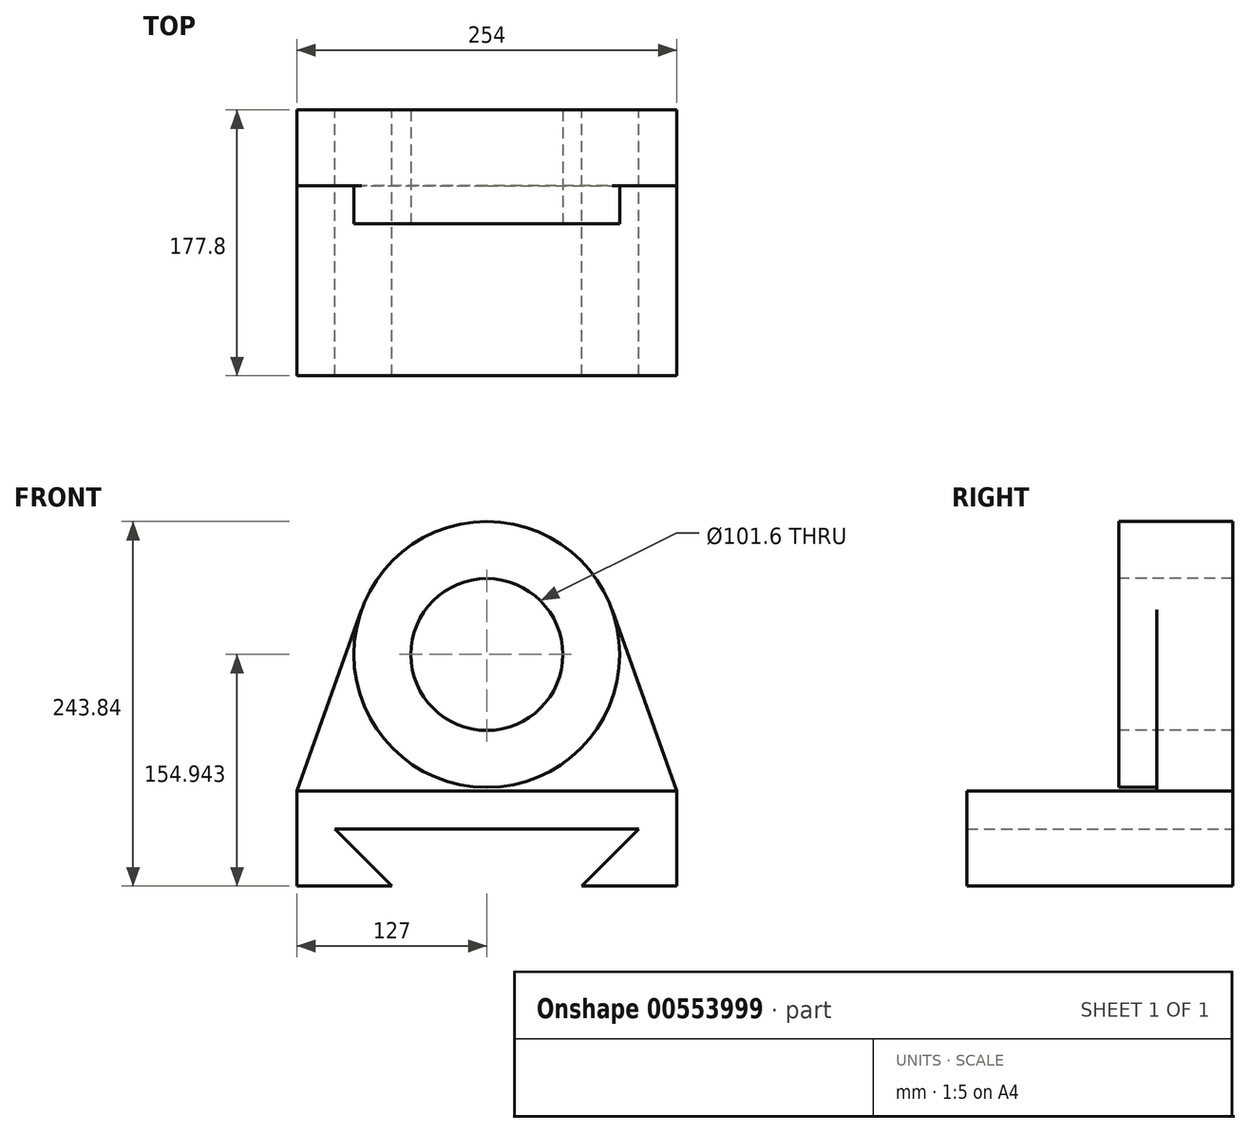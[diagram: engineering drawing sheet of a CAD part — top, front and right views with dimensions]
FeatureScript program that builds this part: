
annotation { "Feature Type Name" : "Feature", "Feature Type Description" : "" }
export const myFeature = defineFeature(function(context is Context, id is Id, definition is map)
    precondition{}
    {
        {
            var Q0;
            Q0=qCreatedBy(makeId("Front.planeOp"),FACE);
            var sketch = newSketch(context, id + "F0", { "sketchPlane" : qUnion([Q0])});
            skLineSegment(sketch, "E0", {"start": v(254, 131.23) * mm, "end": v(0, 131.23) * mm});
            skCircle(sketch, "E1", {"center": v(127, 222.67) * mm, "radius": 50.8 * mm});
            skPoint(sketch, "E1.centerSnap0", {"position": v(127, 131.23) * mm});
            skCircle(sketch, "E2", {"center": v(127, 222.67) * mm, "radius": 88.9 * mm});
            skLineSegment(sketch, "E3", {"start": v(254, 131.23) * mm, "end": v(210.73, 252.54) * mm});
            skLineSegment(sketch, "E4", {"start": v(0, 131.23) * mm, "end": v(43.27, 252.54) * mm});
            skLineSegment(sketch, "E5", {"start": v(190.5, 67.73) * mm, "end": v(228.6, 105.83) * mm});
            skLineSegment(sketch, "E6", {"start": v(228.6, 105.83) * mm, "end": v(25.4, 105.83) * mm});
            skLineSegment(sketch, "E7", {"start": v(25.4, 105.83) * mm, "end": v(63.5, 67.73) * mm});
            skLineSegment(sketch, "E8", {"start": v(63.5, 67.73) * mm, "end": v(63.5, 45) * mm});
            skLineSegment(sketch, "E9", {"start": v(190.5, 67.73) * mm, "end": v(254, 67.73) * mm});
            skLineSegment(sketch, "E10", {"start": v(63.5, 67.73) * mm, "end": v(0, 67.73) * mm});
            skLineSegment(sketch, "E11", {"start": v(0, 131.23) * mm, "end": v(0, 67.73) * mm});
            skLineSegment(sketch, "E12", {"start": v(254, 131.23) * mm, "end": v(254, 67.73) * mm});
            skSolve(sketch);
        }
        {
            var Q0;
            Q0=makeQuery(id+"F0.imprint","IMPRINT",FACE,{"disambiguationData":[TD([[makeQuery(id+"F0.imprint","IMPRINT",EDGE,{"derivedFrom":sQuery(id+"F0.wireOp",EDGE,"E0")}),1.0]])]});
            extrude(context, id + "F1", {"entities" : qUnion([Q0]), "depth" : 127 * mm, "offsetDistance" : 25.4 * mm});
        }
        {
            var Q0;
            Q0=makeQuery(id+"F0.imprint","IMPRINT",FACE,{"disambiguationData":[TD([[makeQuery(id+"F0.imprint","IMPRINT",EDGE,{"derivedFrom":sQuery(id+"F0.wireOp",EDGE,"E1")}),-1.0]])]});
            var Q1;
            Q1=makeQuery(id+"F0.imprint","IMPRINT",FACE,{"disambiguationData":[TD([[makeQuery(id+"F0.imprint","IMPRINT",EDGE,{"derivedFrom":sQuery(id+"F0.wireOp",EDGE,"E0")}),-1.0]])]});
            var Q2;
            Q2=makeQuery(id+"F0.imprint","IMPRINT",FACE,{"disambiguationData":[TD([[makeQuery(id+"F0.imprint","IMPRINT",EDGE,{"derivedFrom":sQuery(id+"F0.wireOp",EDGE,"E0")}),1.0]])]});
            extrude(context, id + "F2", {"entities" : qUnion([Q0, Q1, Q2]), "operationType" : NewBodyOperationType.ADD, "oppositeDirection" : true, "depth" : 50.8 * mm, "offsetDistance" : 25.4 * mm});
        }
        {
            var Q0;
            Q0=makeQuery(id+"F0.imprint","IMPRINT",FACE,{"disambiguationData":[TD([[makeQuery(id+"F0.imprint","IMPRINT",EDGE,{"derivedFrom":sQuery(id+"F0.wireOp",EDGE,"E1")}),-1.0]])]});
            extrude(context, id + "F3", {"entities" : qUnion([Q0]), "operationType" : NewBodyOperationType.ADD, "depth" : 25.4 * mm, "offsetDistance" : 25.4 * mm});
        }
    });
